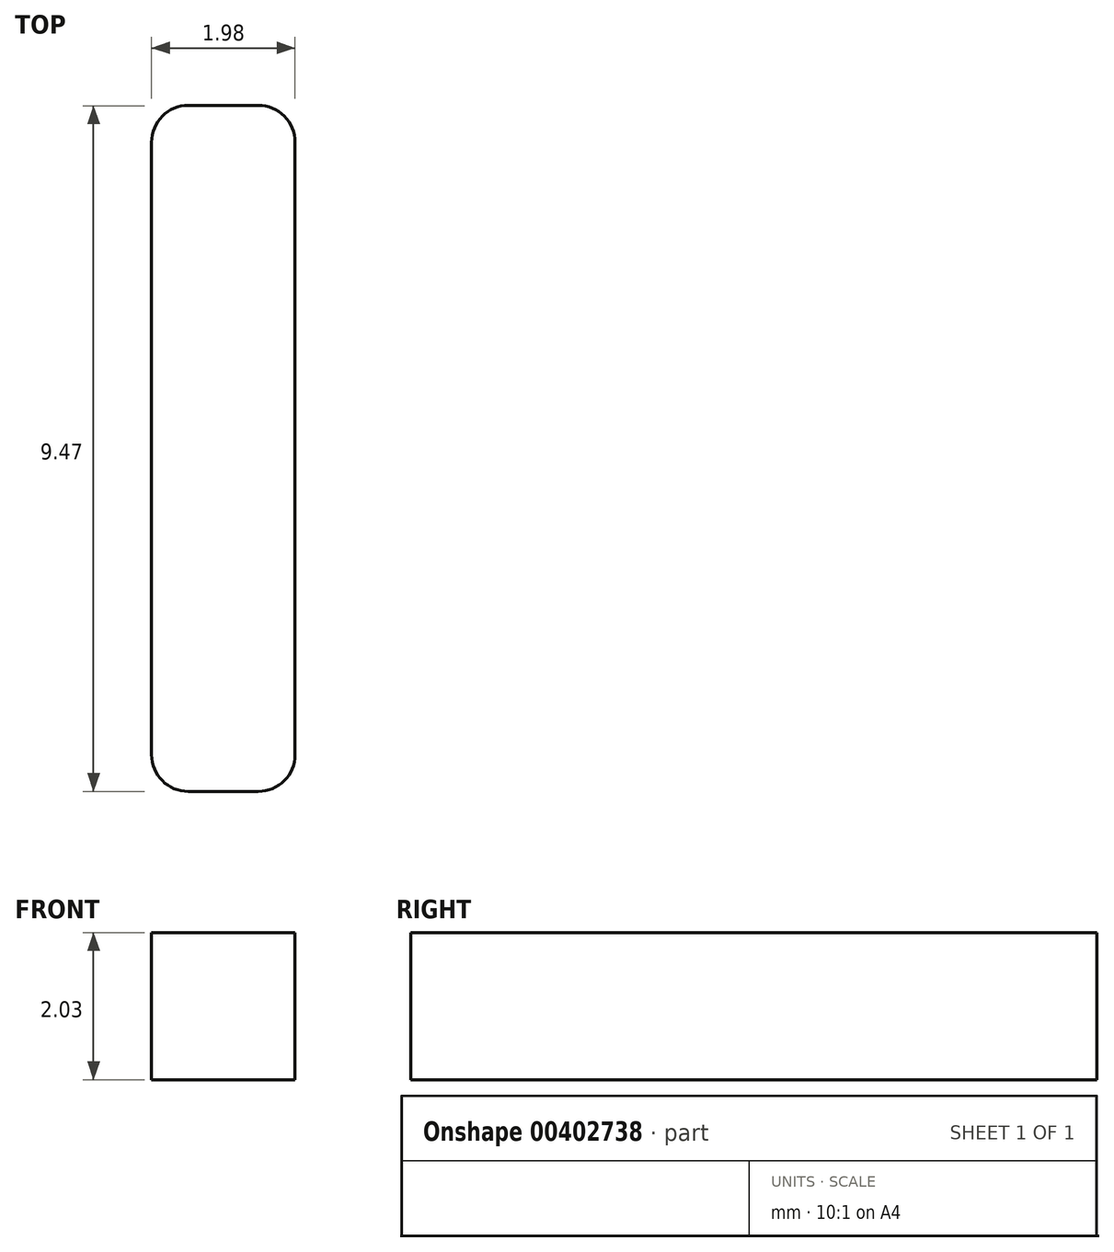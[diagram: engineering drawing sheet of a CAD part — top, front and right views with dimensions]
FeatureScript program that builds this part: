
annotation { "Feature Type Name" : "Feature", "Feature Type Description" : "" }
export const myFeature = defineFeature(function(context is Context, id is Id, definition is map)
    precondition{}
    {
        {
            var Q0;
            Q0=qCreatedBy(makeId("Top.planeOp"),FACE);
            var sketch = newSketch(context, id + "F0", { "sketchPlane" : qUnion([Q0])});
            skLineSegment(sketch, "E0.bottom", {"start": v(0.48, 0) * mm, "end": v(-0.48, 0) * mm});
            skLineSegment(sketch, "E0.top", {"start": v(0.48, 9.47) * mm, "end": v(-0.48, 9.47) * mm});
            skLineSegment(sketch, "E0.left", {"start": v(1, 0.5) * mm, "end": v(1, 8.97) * mm});
            skLineSegment(sketch, "E0.right", {"start": v(-1, 0.5) * mm, "end": v(-1, 8.97) * mm});
            skPoint(sketch, "E1", {"position": v(0, 0) * mm});
            skLineSegment(sketch, "E2", {"start": v(0, -1.94) * mm, "end": v(0, 14.4) * mm, "construction": true});
            skPoint(sketch, "E3.visualSharp", {"position": v(1, 0) * mm});
            skArc(sketch, "E3.filletArc", {"start": v(0.48, 0) * mm, "mid": v(0.84, 0.15) * mm, "end": v(1, 0.5) * mm});
            skPoint(sketch, "E4.visualSharp", {"position": v(-1, 0) * mm});
            skArc(sketch, "E4.filletArc", {"start": v(-1, 0.5) * mm, "mid": v(-0.84, 0.15) * mm, "end": v(-0.48, 0) * mm});
            skPoint(sketch, "E5.visualSharp", {"position": v(-1, 9.47) * mm});
            skArc(sketch, "E5.filletArc", {"start": v(-0.48, 9.47) * mm, "mid": v(-0.84, 9.33) * mm, "end": v(-1, 8.97) * mm});
            skPoint(sketch, "E6.visualSharp", {"position": v(1, 9.47) * mm});
            skArc(sketch, "E6.filletArc", {"start": v(1, 8.97) * mm, "mid": v(0.84, 9.33) * mm, "end": v(0.48, 9.47) * mm});
            skSolve(sketch);
        }
        {
            var Q0;
            Q0=qSketchRegion(id+"F0",true);
            extrude(context, id + "F1", {"entities" : qUnion([Q0]), "depth" : 2.03 * mm});
        }
    });
